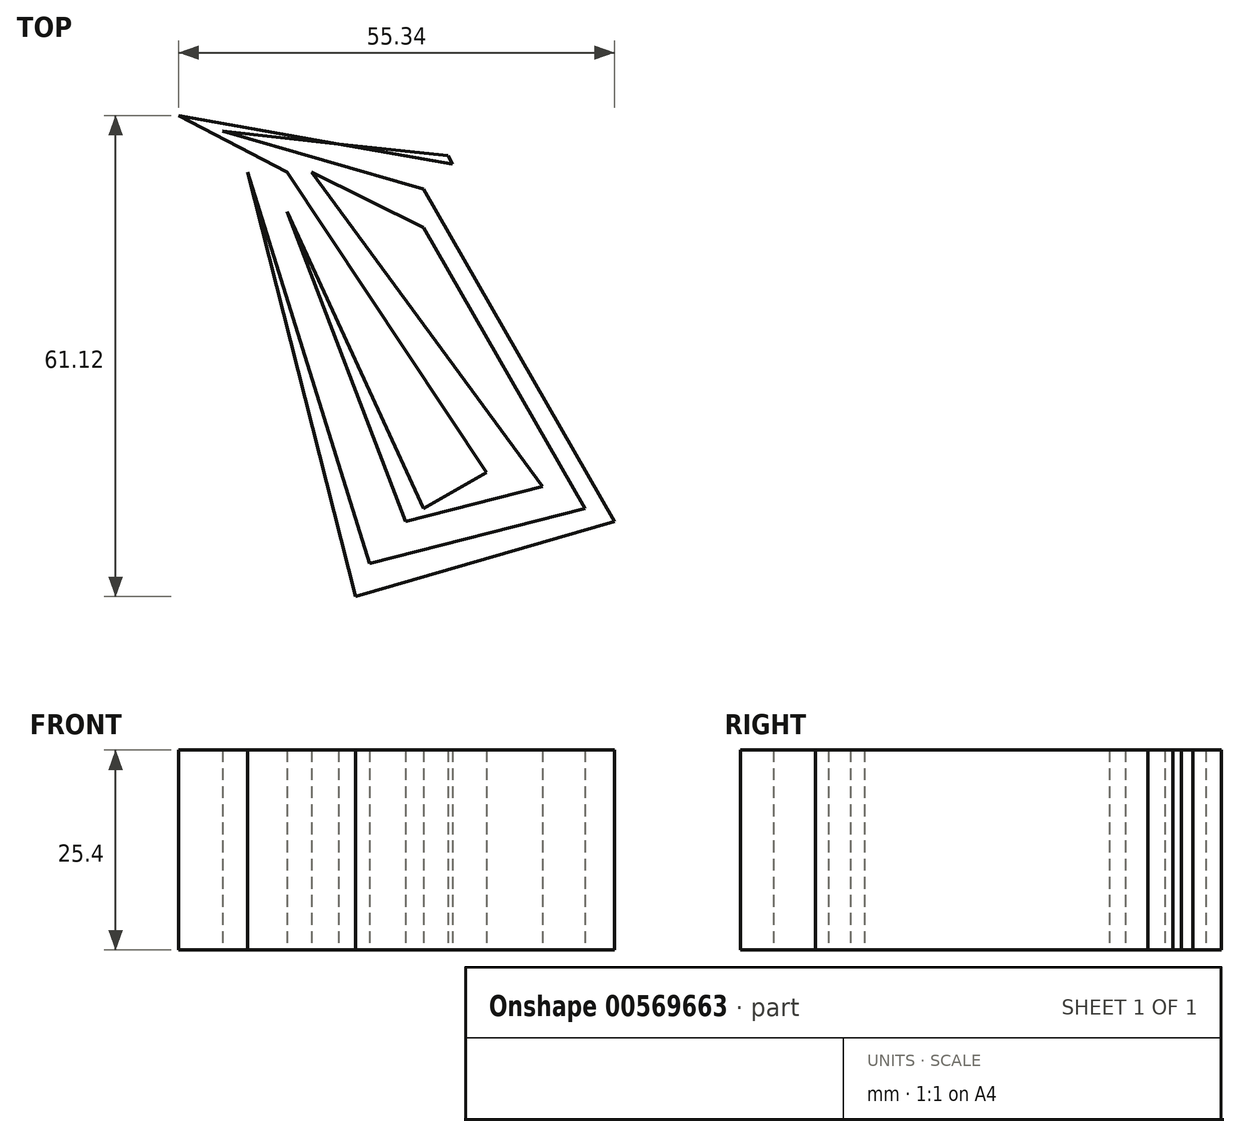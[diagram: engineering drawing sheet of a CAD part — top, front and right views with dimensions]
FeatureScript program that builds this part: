
annotation { "Feature Type Name" : "Feature", "Feature Type Description" : "" }
export const myFeature = defineFeature(function(context is Context, id is Id, definition is map)
    precondition{}
    {
        {
            var Q0;
            Q0=qCreatedBy(makeId("Top.planeOp"),FACE);
            var sketch = newSketch(context, id + "F0", { "sketchPlane" : qUnion([Q0])});
            skLineSegment(sketch, "E0", {"start": v(-33.56, 29.34) * mm, "end": v(-18.67, -29.11) * mm});
            skLineSegment(sketch, "E1", {"start": v(-17.11, -29.11) * mm, "end": v(20.67, -20) * mm});
            skLineSegment(sketch, "E2", {"start": v(20.67, -20) * mm, "end": v(-4.89, 30) * mm});
            skLineSegment(sketch, "E3", {"start": v(-4.89, 30) * mm, "end": v(-33.56, 33.12) * mm});
            skLineSegment(sketch, "E4", {"start": v(-33.56, 33.12) * mm, "end": v(-8, 25.78) * mm});
            skLineSegment(sketch, "E5", {"start": v(-8, 25.78) * mm, "end": v(16.22, -16.45) * mm});
            skLineSegment(sketch, "E6", {"start": v(16.22, -16.45) * mm, "end": v(-16.67, -26) * mm});
            skLineSegment(sketch, "E7", {"start": v(-16.67, -26) * mm, "end": v(-30.77, 29.34) * mm});
            skLineSegment(sketch, "E8", {"start": v(-30.4, 27.9) * mm, "end": v(-14.9, -21.78) * mm});
            skLineSegment(sketch, "E9", {"start": v(-14.9, -21.78) * mm, "end": v(12.48, -14.8) * mm});
            skLineSegment(sketch, "E10", {"start": v(12.48, -14.8) * mm, "end": v(-8, 20.89) * mm});
            skLineSegment(sketch, "E11", {"start": v(-8, 20.89) * mm, "end": v(-22.22, 27.9) * mm});
            skLineSegment(sketch, "E12", {"start": v(-22.22, 27.9) * mm, "end": v(7.11, -12) * mm});
            skLineSegment(sketch, "E13", {"start": v(7.11, -12) * mm, "end": v(-10.34, -16.45) * mm});
            skLineSegment(sketch, "E14", {"start": v(-10.34, -16.45) * mm, "end": v(-25.34, 22.9) * mm});
            skLineSegment(sketch, "E15", {"start": v(-25.34, 22.9) * mm, "end": v(-8, -14.8) * mm});
            skLineSegment(sketch, "E16", {"start": v(-8, -14.8) * mm, "end": v(0, -10.22) * mm});
            skLineSegment(sketch, "E17", {"start": v(0, -10.22) * mm, "end": v(-25.34, 27.9) * mm});
            skLineSegment(sketch, "E18", {"start": v(-25.34, 27.9) * mm, "end": v(-39.12, 35.12) * mm});
            skLineSegment(sketch, "E19", {"start": v(-39.12, 35.12) * mm, "end": v(110.01, 8.67) * mm});
            skLineSegment(sketch, "E20", {"start": v(110.01, 8.67) * mm, "end": v(94.53, 11.41) * mm});
            skSolve(sketch);
        }
        {
            var Q0;
            {var subQ0=sQuery(id+"F0.wireOp",EDGE,"E3");var subQ1=sQuery(id+"F0.wireOp",EDGE,"E2");var subQ2=makeQuery(id+"F0.imprint","INTERSECT",VERTEX,{"derivedFrom":[subQ1,subQ0]});Q0=makeQuery(id+"F0.imprint","IMPRINT",FACE,{"disambiguationData":[TD([[makeQuery(id+"F0.imprint","IMPRINT",EDGE,{"disambiguationData":[TD([[subQ2,1.0]])],"derivedFrom":subQ1}),1.0]])]});}
            var Q1;
            {var subQ3=sQuery(id+"F0.wireOp",EDGE,"E4");Q1=makeQuery(id+"F0.imprint","IMPRINT",FACE,{"disambiguationData":[TD([[makeQuery(id+"F0.imprint","IMPRINT",EDGE,{"derivedFrom":subQ3}),-1.0]])]});}
            extrude(context, id + "F1", {"entities" : qUnion([Q0, Q1]), "depth" : 25.4 * mm, "offsetDistance" : 25.4 * mm});
        }
    });
